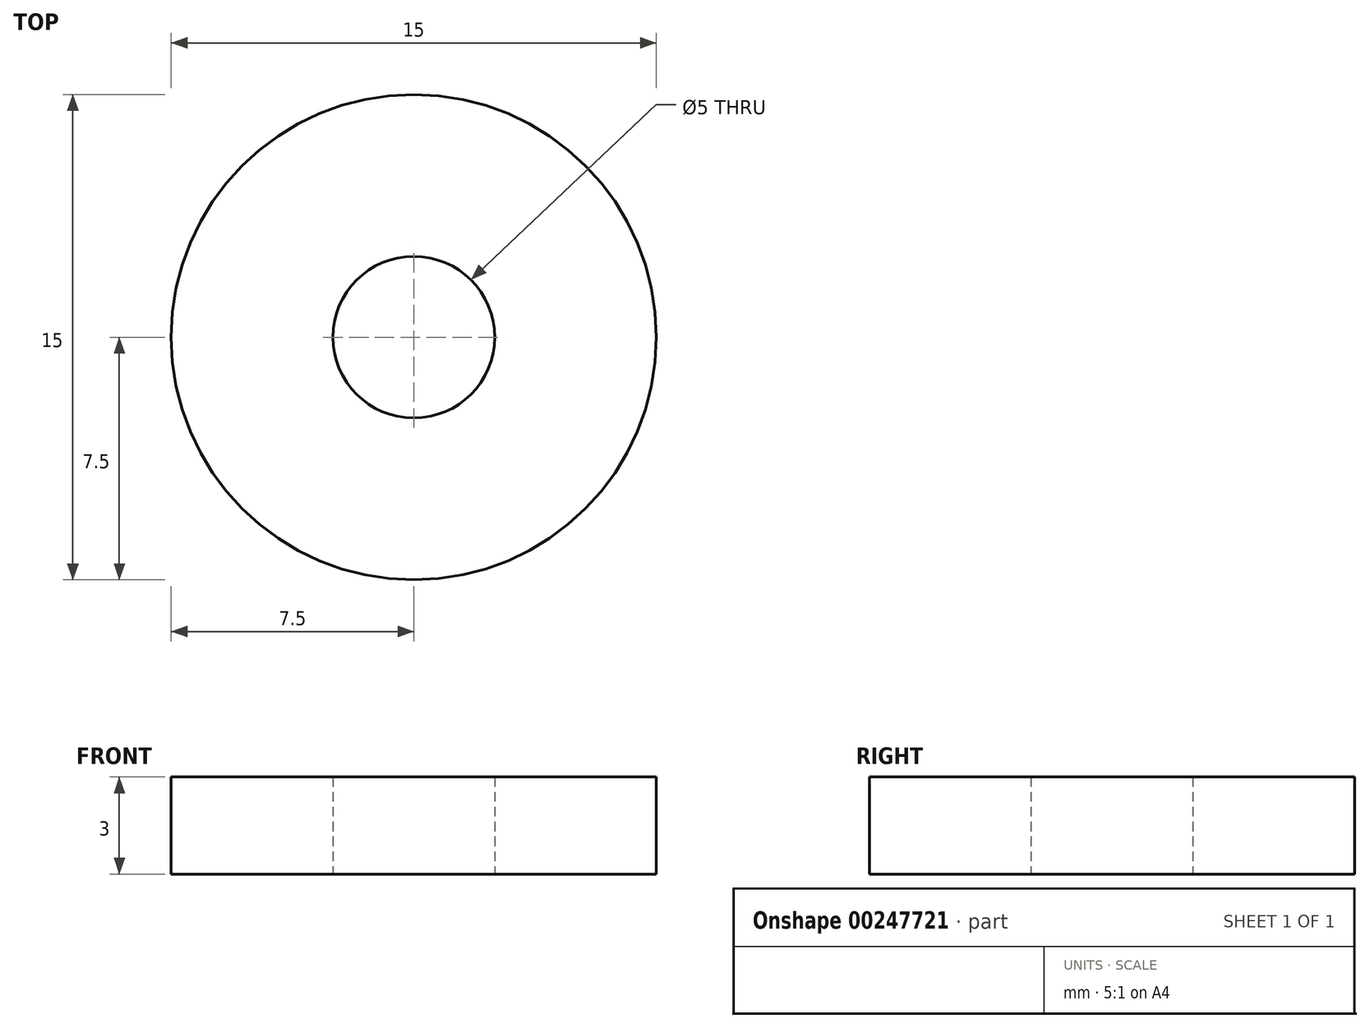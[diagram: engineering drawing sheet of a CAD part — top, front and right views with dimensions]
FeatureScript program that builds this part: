
annotation { "Feature Type Name" : "Feature", "Feature Type Description" : "" }
export const myFeature = defineFeature(function(context is Context, id is Id, definition is map)
    precondition{}
    {
        {
            var Q0;
            Q0=qCreatedBy(makeId("Top.planeOp"),FACE);
            var sketch = newSketch(context, id + "F0", { "sketchPlane" : qUnion([Q0])});
            skCircle(sketch, "E0", {"center": v(0, 0) * mm, "radius": 7.5 * mm});
            skCircle(sketch, "E1", {"center": v(0, 0) * mm, "radius": 2.5 * mm});
            skSolve(sketch);
        }
        {
            var Q0;
            Q0 = qSketchRegion(id + "F0", true);
            extrude(context, id + "F1", {"entities" : qUnion([Q0]), "depth" : 3 * mm});
        }
    });
